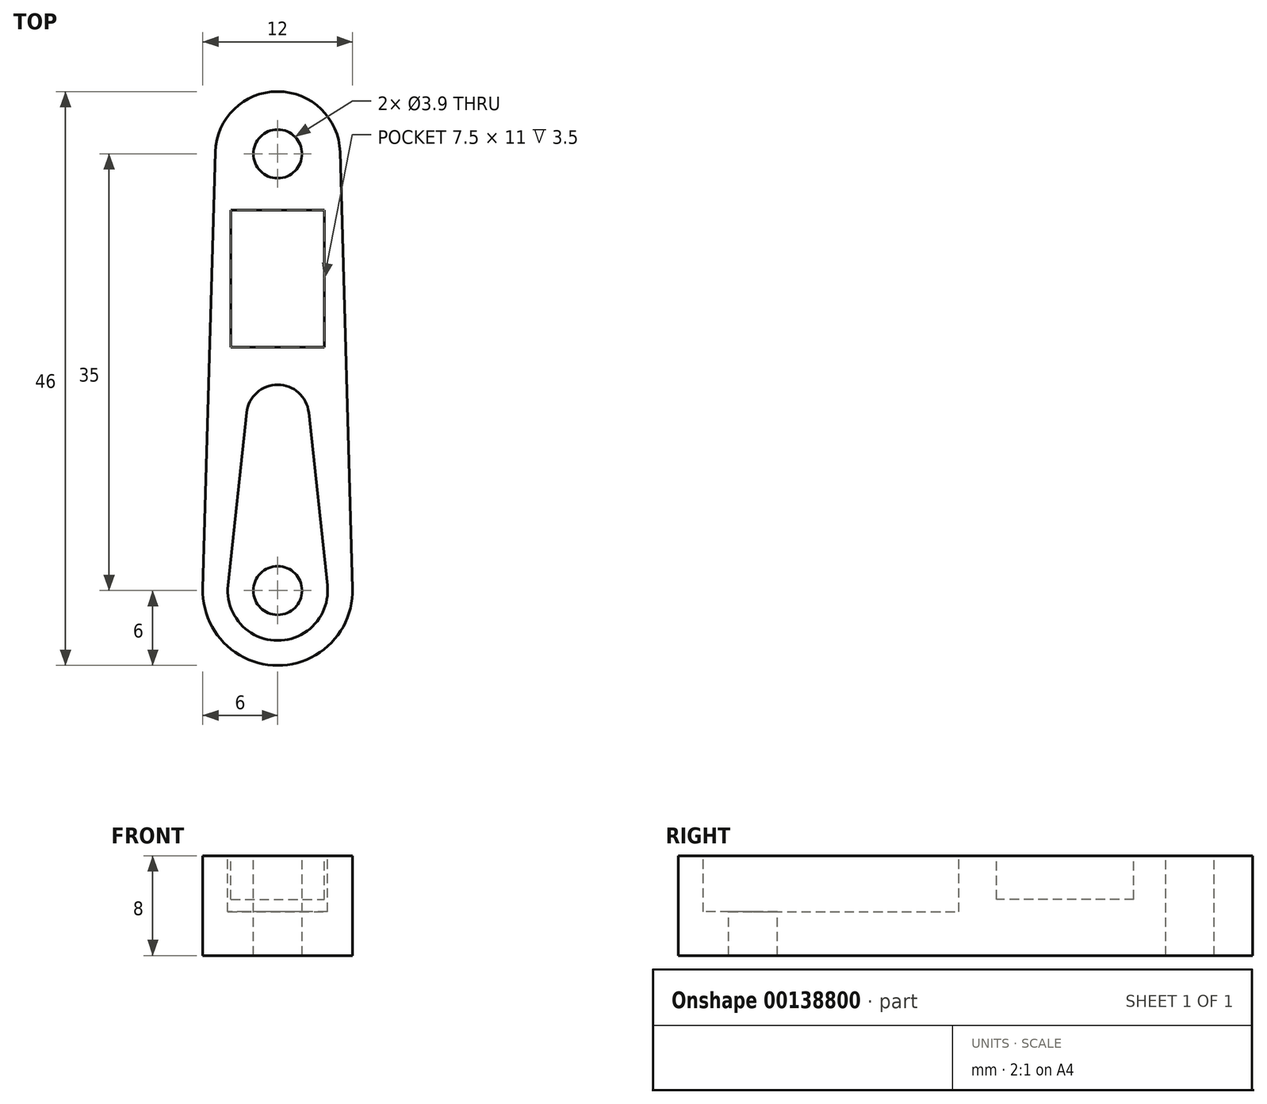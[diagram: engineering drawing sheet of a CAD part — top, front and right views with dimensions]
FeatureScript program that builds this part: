
annotation { "Feature Type Name" : "Feature", "Feature Type Description" : "" }
export const myFeature = defineFeature(function(context is Context, id is Id, definition is map)
    precondition{}
    {
        {
            var Q0;
            Q0=qCreatedBy(makeId("Top.planeOp"),FACE);
            var sketch = newSketch(context, id + "F0", { "sketchPlane" : qUnion([Q0])});
            skCircle(sketch, "E0", {"center": v(0, 0) * mm, "radius": 6 * mm});
            skLineSegment(sketch, "E1", {"start": v(0, 0) * mm, "end": v(0, 35) * mm});
            skCircle(sketch, "E2", {"center": v(0, 35) * mm, "radius": 5 * mm});
            skLineSegment(sketch, "E3", {"start": v(-5, 35.14) * mm, "end": v(-6, 0) * mm});
            skLineSegment(sketch, "E4", {"start": v(5, 35.14) * mm, "end": v(6, 0.17) * mm});
            skSolve(sketch);
        }
        {
            var Q0;
            Q0=qSketchRegion(id+"F0",true);
            extrude(context, id + "F1", {"entities" : qUnion([Q0]), "depth" : 8 * mm});
        }
        {
            var Q0;
            Q0=makeQuery(id+"F1.opExtrude","CAP_FACE",FACE,{"disambiguationData":[OSD([sQuery(id+"F0.wireOp",EDGE,"E0"),sQuery(id+"F0.wireOp",EDGE,"E2"),sQuery(id+"F0.wireOp",EDGE,"E3"),sQuery(id+"F0.wireOp",EDGE,"E4")])],"isStart":false});
            var sketch = newSketch(context, id + "F2", { "sketchPlane" : qUnion([Q0])});
            skCircle(sketch, "E5", {"center": v(0, 0) * mm, "radius": 4 * mm});
            skLineSegment(sketch, "E6", {"start": v(0, 0) * mm, "end": v(0, 14) * mm});
            skCircle(sketch, "E7", {"center": v(0, 14) * mm, "radius": 2.5 * mm});
            skLineSegment(sketch, "E8", {"start": v(-2.49, 14.27) * mm, "end": v(-3.98, 0.43) * mm});
            skLineSegment(sketch, "E9", {"start": v(3.98, 0.43) * mm, "end": v(2.49, 14.27) * mm});
            skSolve(sketch);
        }
        {
            var Q0;
            Q0=qSketchRegion(id+"F2",true);
            extrude(context, id + "F3", {"entities" : qUnion([Q0]), "operationType" : NewBodyOperationType.REMOVE, "oppositeDirection" : true, "depth" : 4.5 * mm});
        }
        {
            var Q0;
            Q0=makeQuery(id+"F3.boolean.opBoolean","COPY",FACE,{"derivedFrom":makeQuery(id+"F3.opExtrude","CAP_FACE",FACE,{"disambiguationData":[OSD([sQuery(id+"F2.wireOp",EDGE,"E5"),sQuery(id+"F2.wireOp",EDGE,"E7"),sQuery(id+"F2.wireOp",EDGE,"E8"),sQuery(id+"F2.wireOp",EDGE,"E9")])],"isStart":false})});
            var sketch = newSketch(context, id + "F4", { "sketchPlane" : qUnion([Q0])});
            skCircle(sketch, "E10", {"center": v(0, 0) * mm, "radius": 1.95 * mm});
            skSolve(sketch);
        }
        {
            var Q0;
            Q0=makeQuery(id+"F4.imprint","IMPRINT",FACE,{"disambiguationData":[TD([[makeQuery(id+"F4.imprint","IMPRINT",EDGE,{"derivedFrom":sQuery(id+"F4.wireOp",EDGE,"E10")}),1.0]])]});
            extrude(context, id + "F5", {"entities" : qUnion([Q0]), "operationType" : NewBodyOperationType.REMOVE, "endBound" : BoundingType.THROUGH_ALL, "oppositeDirection" : true, "depth" : 25 * mm});
        }
        {
            var Q0;
            Q0=makeQuery(id+"F1.opExtrude","CAP_FACE",FACE,{"disambiguationData":[OSD([sQuery(id+"F0.wireOp",EDGE,"E0"),sQuery(id+"F0.wireOp",EDGE,"E2"),sQuery(id+"F0.wireOp",EDGE,"E3"),sQuery(id+"F0.wireOp",EDGE,"E4")])],"isStart":false});
            var sketch = newSketch(context, id + "F6", { "sketchPlane" : qUnion([Q0])});
            skCircle(sketch, "E11", {"center": v(0, 35) * mm, "radius": 1.95 * mm});
            skSolve(sketch);
        }
        {
            var Q0;
            Q0=makeQuery(id+"F6.imprint","IMPRINT",FACE,{"disambiguationData":[TD([[makeQuery(id+"F6.imprint","IMPRINT",EDGE,{"derivedFrom":sQuery(id+"F6.wireOp",EDGE,"E11")}),1.0]])]});
            extrude(context, id + "F7", {"entities" : qUnion([Q0]), "operationType" : NewBodyOperationType.REMOVE, "endBound" : BoundingType.THROUGH_ALL, "oppositeDirection" : true, "depth" : 25 * mm});
        }
        {
            var Q0;
            Q0=makeQuery(id+"F1.opExtrude","CAP_FACE",FACE,{"disambiguationData":[OSD([sQuery(id+"F0.wireOp",EDGE,"E0"),sQuery(id+"F0.wireOp",EDGE,"E2"),sQuery(id+"F0.wireOp",EDGE,"E3"),sQuery(id+"F0.wireOp",EDGE,"E4")])],"isStart":false});
            var sketch = newSketch(context, id + "F8", { "sketchPlane" : qUnion([Q0])});
            skLineSegment(sketch, "E12.bottom", {"start": v(-3.75, 30.5) * mm, "end": v(3.75, 30.5) * mm});
            skLineSegment(sketch, "E12.top", {"start": v(-3.75, 19.5) * mm, "end": v(3.75, 19.5) * mm});
            skLineSegment(sketch, "E12.left", {"start": v(-3.75, 30.5) * mm, "end": v(-3.75, 19.5) * mm});
            skLineSegment(sketch, "E12.right", {"start": v(3.75, 30.5) * mm, "end": v(3.75, 19.5) * mm});
            skSolve(sketch);
        }
        {
            var Q0;
            Q0=qSketchRegion(id+"F8",true);
            extrude(context, id + "F9", {"entities" : qUnion([Q0]), "operationType" : NewBodyOperationType.REMOVE, "oppositeDirection" : true, "depth" : 3.5 * mm});
        }
    });
